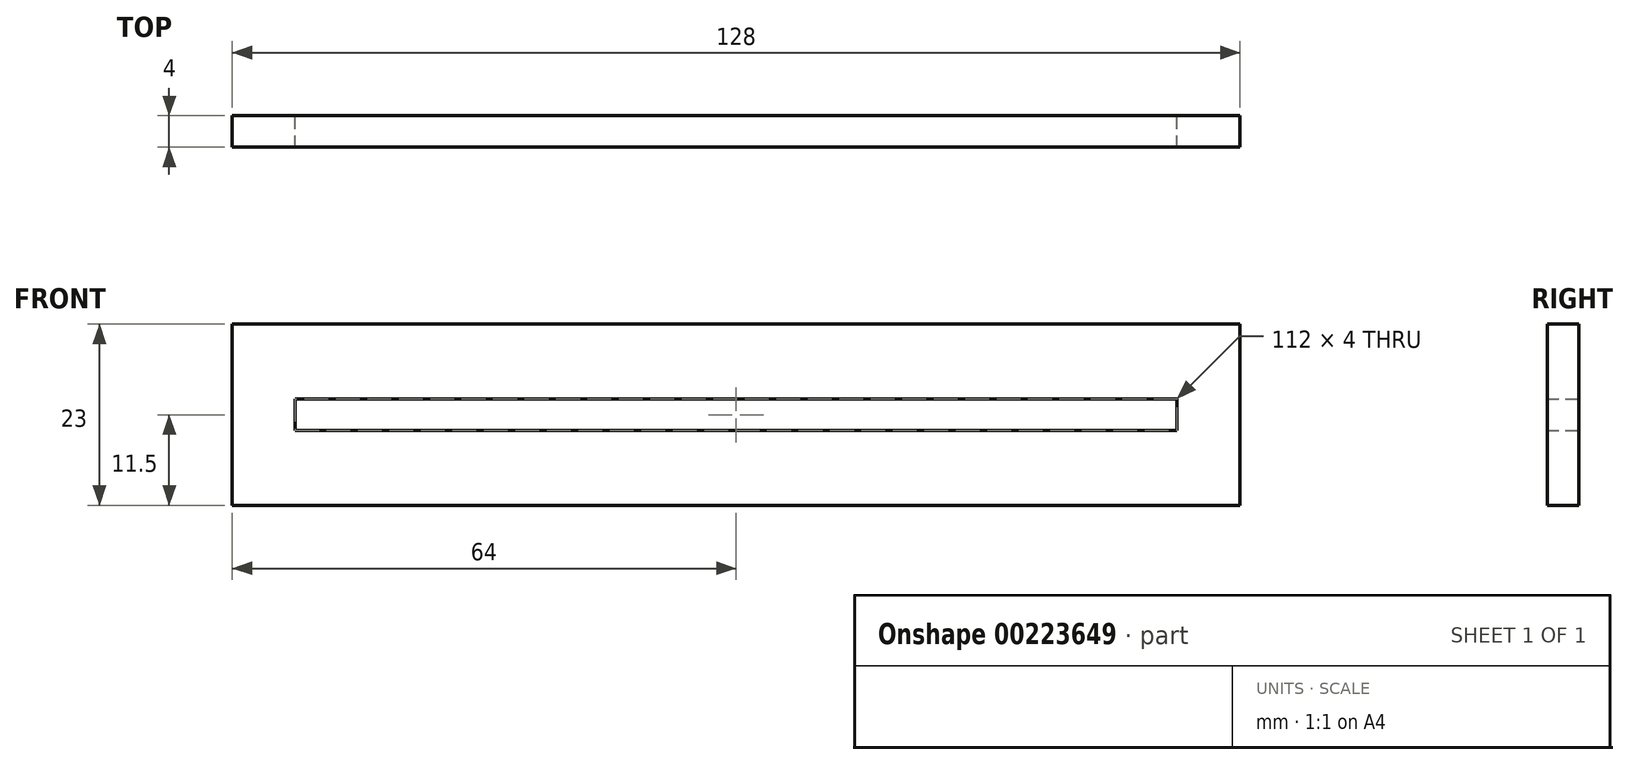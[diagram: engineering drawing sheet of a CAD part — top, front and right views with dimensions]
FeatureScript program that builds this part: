
annotation { "Feature Type Name" : "Feature", "Feature Type Description" : "" }
export const myFeature = defineFeature(function(context is Context, id is Id, definition is map)
    precondition{}
    {
        {
            var Q0;
            Q0=qCreatedBy(makeId("Front.planeOp"),FACE);
            var sketch = newSketch(context, id + "F0", { "sketchPlane" : qUnion([Q0])});
            skLineSegment(sketch, "E0", {"start": v(0, 0) * mm, "end": v(128, 0) * mm});
            skLineSegment(sketch, "E1", {"start": v(128, 0) * mm, "end": v(128, -23) * mm});
            skLineSegment(sketch, "E2", {"start": v(128, -23) * mm, "end": v(0, -23) * mm});
            skLineSegment(sketch, "E3", {"start": v(0, -23) * mm, "end": v(0, 0) * mm});
            skLineSegment(sketch, "E4", {"start": v(128, -11.5) * mm, "end": v(128, 0) * mm});
            skLineSegment(sketch, "E5", {"start": v(128, -11.5) * mm, "end": v(128, -13.5) * mm});
            skLineSegment(sketch, "E6", {"start": v(128, -11.5) * mm, "end": v(128, -9.5) * mm});
            skPoint(sketch, "E6.endSnap0", {"position": v(128, -5.75) * mm});
            skPoint(sketch, "E7.endSnap0", {"position": v(0, -11.5) * mm});
            skLineSegment(sketch, "E8", {"start": v(8, -9.5) * mm, "end": v(8, -13.5) * mm});
            skLineSegment(sketch, "E9", {"start": v(120, -9.5) * mm, "end": v(120, -13.5) * mm});
            skLineSegment(sketch, "E10", {"start": v(8, -9.5) * mm, "end": v(120, -9.5) * mm});
            skLineSegment(sketch, "E11", {"start": v(120, -13.5) * mm, "end": v(8, -13.5) * mm});
            skSolve(sketch);
        }
        {
            var Q0;
            Q0=makeQuery(id+"F0.imprint","IMPRINT",FACE,{"disambiguationData":[TD([[makeQuery(id+"F0.imprint","IMPRINT",EDGE,{"derivedFrom":sQuery(id+"F0.wireOp",EDGE,"E0")}),-1.0]])]});
            extrude(context, id + "F1", {"entities" : qUnion([Q0]), "depth" : 4 * mm});
        }
    });
